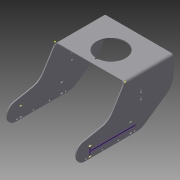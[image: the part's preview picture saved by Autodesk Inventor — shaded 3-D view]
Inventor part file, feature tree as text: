
AUTODESK INVENTOR PART (.ipt)
format: ipt  version: 2015 (Build 190159000, 159)  size: 397,312 bytes
history: native  units: mm
features: sketch x5, other x2, extrude x1
ambient origin geometry x8: Origin, YZ Plane, XZ Plane, XY Plane, X Axis, Y Axis, Z Axis, Center Point
bodies: Body1 (feature_tree)
feature tree (8):
  extrude  "Extrusion25"  Depth=3.0mm TaperAngle=0.0deg
  other  "Bend Part37"
  other  "Bend Part38"
  sketch  "Sketch47"  dims[d813=5.0mm d814=90.0deg]
  sketch  "Sketch48"
  sketch  "Sketch44"  dims[d19=5.0mm d127=97.0mm d151=5.0mm d163=5.0mm d222=5.0mm d248=40.0mm d294=25.0mm d324=5.0mm d326=25.0mm d329=25.0mm d344=6.0mm d358=6.0mm d404=5.0mm d406=45.0mm d445=20.0mm d446=30.0mm d448=45.0deg d460=5.606189mm d463=30.0deg d467=42.0mm d468=36.0mm d469=150.0deg d483=12.0mm d486=42.0mm d487=150.0deg d488=36.0mm d489=150.0deg d528=20.0mm d530=65.0mm]
  sketch  "Sketch45"  dims[d726=80.0mm d727=50.0mm d728=200.0mm d729=100.0mm d730=70.0mm d731=180.0mm d732=20.0mm d733=100.0mm d734=50.0mm d735=50.0mm d736=25.0mm d737=5.0mm d738=5.0mm d739=150.0mm d740=5.0mm d741=5.0mm d742=30.0mm d743=10.0mm d744=6.0mm d745=97.0mm d746=73.0mm d747=4.0mm d748=8.0mm d749=8.0mm d750=7.0mm d751=4.0mm d752=8.0mm d753=8.0mm d754=1.0mm d755=8.0mm d756=4.0mm d757=7.0mm d758=8.0mm d759=4.0mm d760=8.0mm d761=30.0mm d762=8.0mm d763=1.0mm d764=30.0mm d765=8.0mm d766=4.0mm d767=8.0mm d768=4.0mm d769=30.0mm d770=7.0mm d771=5.0mm d772=8.0mm d773=4.0mm d774=8.0mm d775=4.0mm d776=30.0mm d777=7.0mm d778=5.0mm d779=90.0mm d780=97.0mm d781=6.0mm d782=10.0mm d783=73.0mm d784=65.0mm d785=100.0mm d786=200.0mm d787=5.0mm d788=2.5mm d789=50.0mm d790=2.5mm d791=5.0mm d792=5.0mm d793=50.0mm d794=5.0mm d795=5.0mm d796=50.0mm d797=5.0mm d798=5.0mm d799=50.0mm d800=5.0mm d801=5.0mm d802=50.0mm d803=10.0mm d804=6.0mm d805=10.0mm d806=10.0mm d807=10.0mm d808=6.0mm d809=3.0mm d810=0.0mm]
  sketch  "Sketch46"  dims[d811=5.0mm d812=90.0deg]
